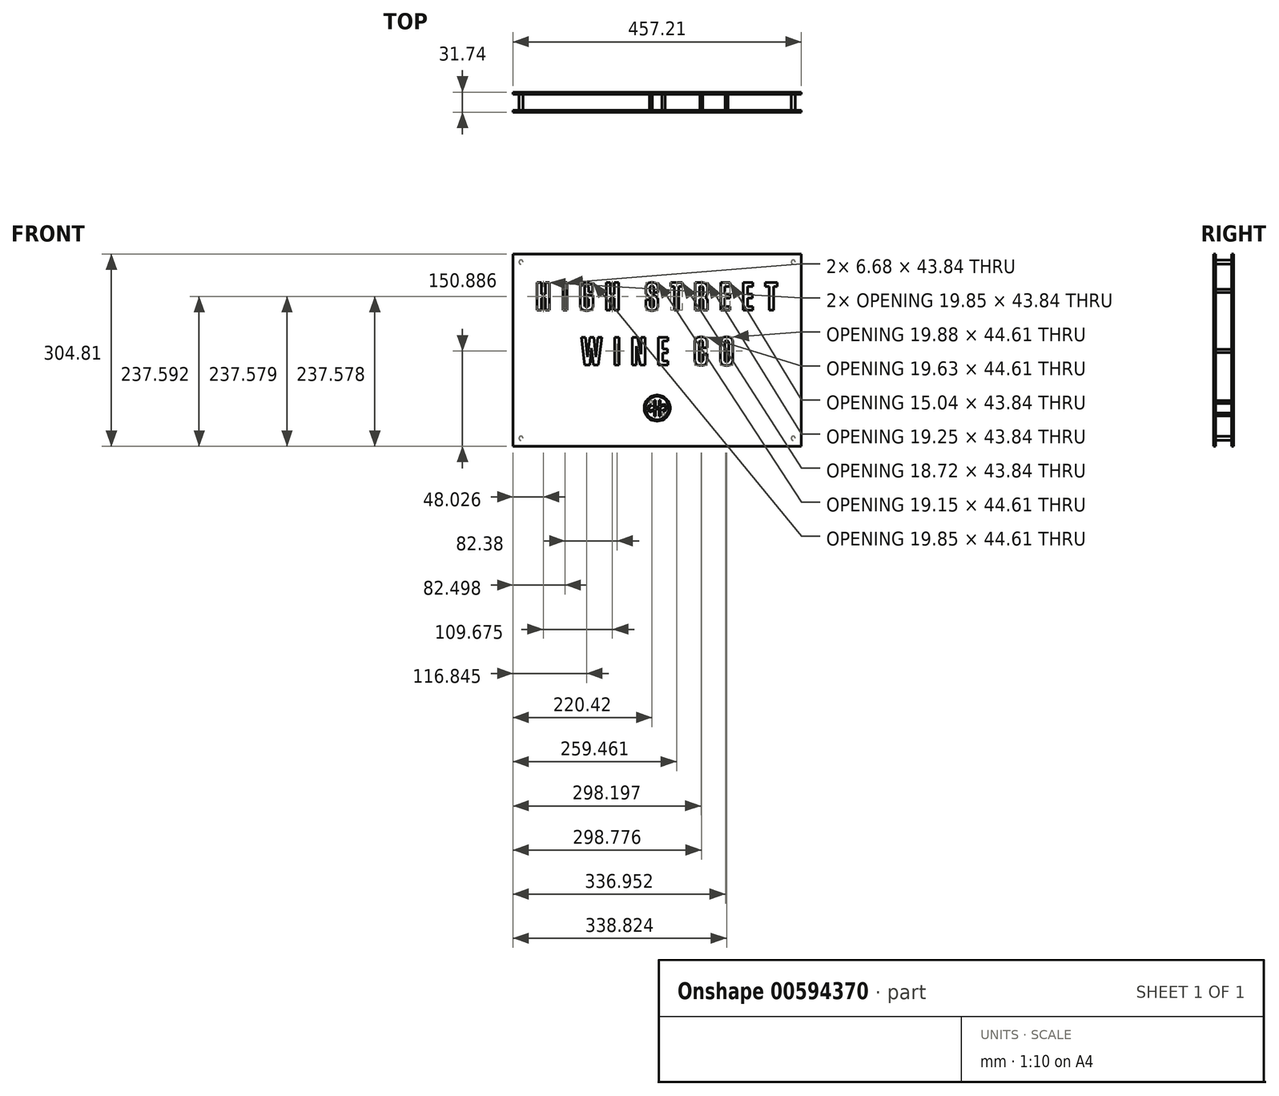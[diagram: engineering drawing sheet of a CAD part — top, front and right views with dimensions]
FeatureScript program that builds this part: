
annotation { "Feature Type Name" : "Feature", "Feature Type Description" : "" }
export const myFeature = defineFeature(function(context is Context, id is Id, definition is map)
    precondition{}
    {
        {
            var Q0;
            Q0=qCreatedBy(makeId("Front.planeOp"),FACE);
            var sketch = newSketch(context, id + "F0", { "sketchPlane" : qUnion([Q0])});
            skLineSegment(sketch, "E0", {"start": v(-228.6, 152.4) * mm, "end": v(228.6, 152.4) * mm});
            skLineSegment(sketch, "E1", {"start": v(228.6, 152.4) * mm, "end": v(228.6, -152.4) * mm});
            skLineSegment(sketch, "E2", {"start": v(228.6, -152.4) * mm, "end": v(-228.6, -152.4) * mm});
            skLineSegment(sketch, "E3", {"start": v(-228.6, -152.4) * mm, "end": v(-228.6, 152.4) * mm});
            skLineSegment(sketch, "E4", {"start": v(-177.33, 88.62) * mm, "end": v(-177.33, 107.1) * mm});
            skLineSegment(sketch, "E5", {"start": v(-177.33, 107.1) * mm, "end": v(-170.65, 107.1) * mm});
            skLineSegment(sketch, "E6", {"start": v(-170.65, 107.1) * mm, "end": v(-170.65, 63.26) * mm});
            skLineSegment(sketch, "E7", {"start": v(-170.65, 63.26) * mm, "end": v(-177.33, 63.26) * mm});
            skLineSegment(sketch, "E8", {"start": v(-177.33, 63.26) * mm, "end": v(-177.33, 82.54) * mm});
            skLineSegment(sketch, "E9", {"start": v(-177.33, 82.54) * mm, "end": v(-183.81, 82.54) * mm});
            skLineSegment(sketch, "E10", {"start": v(-183.81, 82.54) * mm, "end": v(-183.81, 63.26) * mm});
            skLineSegment(sketch, "E11", {"start": v(-183.81, 63.26) * mm, "end": v(-190.5, 63.26) * mm});
            skLineSegment(sketch, "E12", {"start": v(-190.5, 63.26) * mm, "end": v(-190.5, 107.1) * mm});
            skLineSegment(sketch, "E13", {"start": v(-190.5, 107.1) * mm, "end": v(-183.81, 107.1) * mm});
            skLineSegment(sketch, "E14", {"start": v(-183.81, 107.1) * mm, "end": v(-183.81, 88.62) * mm});
            skLineSegment(sketch, "E15", {"start": v(-183.81, 88.62) * mm, "end": v(-177.33, 88.62) * mm});
            skLineSegment(sketch, "E16", {"start": v(-149.44, 107.1) * mm, "end": v(-142.76, 107.1) * mm});
            skLineSegment(sketch, "E17", {"start": v(-142.76, 107.1) * mm, "end": v(-142.76, 63.26) * mm});
            skLineSegment(sketch, "E18", {"start": v(-142.76, 63.26) * mm, "end": v(-149.44, 63.26) * mm});
            skLineSegment(sketch, "E19", {"start": v(-149.44, 63.26) * mm, "end": v(-149.44, 107.1) * mm});
            skLineSegment(sketch, "E20", {"start": v(-111.87, 81.41) * mm, "end": v(-111.87, 87.2) * mm});
            skLineSegment(sketch, "E21", {"start": v(-111.87, 87.2) * mm, "end": v(-101.83, 87.2) * mm});
            skLineSegment(sketch, "E22", {"start": v(-101.83, 87.2) * mm, "end": v(-101.83, 71.02) * mm});
            skLineSegment(sketch, "E23", {"start": v(-101.83, 71.02) * mm, "end": v(-101.83, 70.13) * mm});
            skLineSegment(sketch, "E24", {"start": v(-101.83, 70.13) * mm, "end": v(-102.34, 67.45) * mm});
            skLineSegment(sketch, "E25", {"start": v(-102.34, 67.45) * mm, "end": v(-103.86, 64.9) * mm});
            skLineSegment(sketch, "E26", {"start": v(-103.86, 64.9) * mm, "end": v(-106.41, 63.37) * mm});
            skLineSegment(sketch, "E27", {"start": v(-106.41, 63.37) * mm, "end": v(-109.1, 62.86) * mm});
            skLineSegment(sketch, "E28", {"start": v(-109.1, 62.86) * mm, "end": v(-110, 62.86) * mm});
            skLineSegment(sketch, "E29", {"start": v(-110, 62.86) * mm, "end": v(-113.54, 62.86) * mm});
            skLineSegment(sketch, "E30", {"start": v(-113.54, 62.86) * mm, "end": v(-114.44, 62.86) * mm});
            skLineSegment(sketch, "E31", {"start": v(-114.44, 62.86) * mm, "end": v(-117.1, 63.37) * mm});
            skLineSegment(sketch, "E32", {"start": v(-117.1, 63.37) * mm, "end": v(-119.65, 64.9) * mm});
            skLineSegment(sketch, "E33", {"start": v(-119.65, 64.9) * mm, "end": v(-121.17, 67.45) * mm});
            skLineSegment(sketch, "E34", {"start": v(-121.17, 67.45) * mm, "end": v(-121.68, 70.13) * mm});
            skLineSegment(sketch, "E35", {"start": v(-121.68, 70.13) * mm, "end": v(-121.68, 71.02) * mm});
            skLineSegment(sketch, "E36", {"start": v(-121.68, 71.02) * mm, "end": v(-121.68, 99.34) * mm});
            skLineSegment(sketch, "E37", {"start": v(-121.68, 99.34) * mm, "end": v(-121.68, 100.23) * mm});
            skLineSegment(sketch, "E38", {"start": v(-121.68, 100.23) * mm, "end": v(-121.17, 102.9) * mm});
            skLineSegment(sketch, "E39", {"start": v(-121.17, 102.9) * mm, "end": v(-119.65, 105.44) * mm});
            skLineSegment(sketch, "E40", {"start": v(-119.65, 105.44) * mm, "end": v(-117.1, 106.97) * mm});
            skLineSegment(sketch, "E41", {"start": v(-117.1, 106.97) * mm, "end": v(-114.44, 107.47) * mm});
            skLineSegment(sketch, "E42", {"start": v(-114.44, 107.47) * mm, "end": v(-113.54, 107.47) * mm});
            skLineSegment(sketch, "E43", {"start": v(-113.54, 107.47) * mm, "end": v(-110.04, 107.47) * mm});
            skLineSegment(sketch, "E44", {"start": v(-110.04, 107.47) * mm, "end": v(-109.15, 107.47) * mm});
            skLineSegment(sketch, "E45", {"start": v(-109.15, 107.47) * mm, "end": v(-106.48, 106.97) * mm});
            skLineSegment(sketch, "E46", {"start": v(-106.48, 106.97) * mm, "end": v(-103.96, 105.45) * mm});
            skLineSegment(sketch, "E47", {"start": v(-103.96, 105.45) * mm, "end": v(-102.46, 102.92) * mm});
            skLineSegment(sketch, "E48", {"start": v(-102.46, 102.92) * mm, "end": v(-101.96, 100.27) * mm});
            skLineSegment(sketch, "E49", {"start": v(-101.96, 100.27) * mm, "end": v(-101.96, 99.39) * mm});
            skLineSegment(sketch, "E50", {"start": v(-101.96, 99.39) * mm, "end": v(-101.96, 92.33) * mm});
            skLineSegment(sketch, "E51", {"start": v(-101.96, 92.33) * mm, "end": v(-108.54, 92.33) * mm});
            skLineSegment(sketch, "E52", {"start": v(-108.54, 92.33) * mm, "end": v(-108.54, 99.01) * mm});
            skLineSegment(sketch, "E53", {"start": v(-108.54, 99.01) * mm, "end": v(-108.54, 99.3) * mm});
            skLineSegment(sketch, "E54", {"start": v(-108.54, 99.3) * mm, "end": v(-108.7, 100.15) * mm});
            skLineSegment(sketch, "E55", {"start": v(-108.7, 100.15) * mm, "end": v(-109.15, 100.96) * mm});
            skLineSegment(sketch, "E56", {"start": v(-109.15, 100.96) * mm, "end": v(-109.93, 101.43) * mm});
            skLineSegment(sketch, "E57", {"start": v(-109.93, 101.43) * mm, "end": v(-110.77, 101.6) * mm});
            skLineSegment(sketch, "E58", {"start": v(-110.77, 101.6) * mm, "end": v(-111.04, 101.6) * mm});
            skLineSegment(sketch, "E59", {"start": v(-111.04, 101.6) * mm, "end": v(-112.44, 101.6) * mm});
            skLineSegment(sketch, "E60", {"start": v(-112.44, 101.6) * mm, "end": v(-112.73, 101.6) * mm});
            skLineSegment(sketch, "E61", {"start": v(-112.73, 101.6) * mm, "end": v(-113.58, 101.43) * mm});
            skLineSegment(sketch, "E62", {"start": v(-113.58, 101.43) * mm, "end": v(-114.38, 100.96) * mm});
            skLineSegment(sketch, "E63", {"start": v(-114.38, 100.96) * mm, "end": v(-114.85, 100.15) * mm});
            skLineSegment(sketch, "E64", {"start": v(-114.85, 100.15) * mm, "end": v(-115, 99.3) * mm});
            skLineSegment(sketch, "E65", {"start": v(-115, 99.3) * mm, "end": v(-115, 99.01) * mm});
            skLineSegment(sketch, "E66", {"start": v(-115, 99.01) * mm, "end": v(-115, 71.33) * mm});
            skLineSegment(sketch, "E67", {"start": v(-115, 71.33) * mm, "end": v(-115, 71.04) * mm});
            skLineSegment(sketch, "E68", {"start": v(-115, 71.04) * mm, "end": v(-114.85, 70.19) * mm});
            skLineSegment(sketch, "E69", {"start": v(-114.85, 70.19) * mm, "end": v(-114.38, 69.4) * mm});
            skLineSegment(sketch, "E70", {"start": v(-114.38, 69.4) * mm, "end": v(-113.58, 68.92) * mm});
            skLineSegment(sketch, "E71", {"start": v(-113.58, 68.92) * mm, "end": v(-112.73, 68.77) * mm});
            skLineSegment(sketch, "E72", {"start": v(-112.73, 68.77) * mm, "end": v(-112.44, 68.77) * mm});
            skLineSegment(sketch, "E73", {"start": v(-112.44, 68.77) * mm, "end": v(-110.94, 68.77) * mm});
            skLineSegment(sketch, "E74", {"start": v(-110.94, 68.77) * mm, "end": v(-110.66, 68.77) * mm});
            skLineSegment(sketch, "E75", {"start": v(-110.66, 68.77) * mm, "end": v(-109.8, 68.92) * mm});
            skLineSegment(sketch, "E76", {"start": v(-109.8, 68.92) * mm, "end": v(-109, 69.4) * mm});
            skLineSegment(sketch, "E77", {"start": v(-109, 69.4) * mm, "end": v(-108.52, 70.19) * mm});
            skLineSegment(sketch, "E78", {"start": v(-108.52, 70.19) * mm, "end": v(-108.36, 71.04) * mm});
            skLineSegment(sketch, "E79", {"start": v(-108.36, 71.04) * mm, "end": v(-108.36, 71.33) * mm});
            skLineSegment(sketch, "E80", {"start": v(-108.36, 71.33) * mm, "end": v(-108.36, 81.41) * mm});
            skLineSegment(sketch, "E81", {"start": v(-108.36, 81.41) * mm, "end": v(-111.87, 81.41) * mm});
            skLineSegment(sketch, "E82", {"start": v(-67.66, 88.62) * mm, "end": v(-67.66, 107.1) * mm});
            skLineSegment(sketch, "E83", {"start": v(-67.66, 107.1) * mm, "end": v(-60.97, 107.1) * mm});
            skLineSegment(sketch, "E84", {"start": v(-60.97, 107.1) * mm, "end": v(-60.97, 63.26) * mm});
            skLineSegment(sketch, "E85", {"start": v(-60.97, 63.26) * mm, "end": v(-67.66, 63.26) * mm});
            skLineSegment(sketch, "E86", {"start": v(-67.66, 63.26) * mm, "end": v(-67.66, 82.54) * mm});
            skLineSegment(sketch, "E87", {"start": v(-67.66, 82.54) * mm, "end": v(-74.14, 82.54) * mm});
            skLineSegment(sketch, "E88", {"start": v(-74.14, 82.54) * mm, "end": v(-74.14, 63.26) * mm});
            skLineSegment(sketch, "E89", {"start": v(-74.14, 63.26) * mm, "end": v(-80.83, 63.26) * mm});
            skLineSegment(sketch, "E90", {"start": v(-80.83, 63.26) * mm, "end": v(-80.83, 107.1) * mm});
            skLineSegment(sketch, "E91", {"start": v(-80.83, 107.1) * mm, "end": v(-74.14, 107.1) * mm});
            skLineSegment(sketch, "E92", {"start": v(-74.14, 107.1) * mm, "end": v(-74.14, 88.62) * mm});
            skLineSegment(sketch, "E93", {"start": v(-74.14, 88.62) * mm, "end": v(-67.66, 88.62) * mm});
            skLineSegment(sketch, "E94", {"start": v(1.4, 78.16) * mm, "end": v(1.4, 71.02) * mm});
            skLineSegment(sketch, "E95", {"start": v(1.4, 71.02) * mm, "end": v(1.4, 70.13) * mm});
            skLineSegment(sketch, "E96", {"start": v(1.4, 70.13) * mm, "end": v(0.9, 67.45) * mm});
            skLineSegment(sketch, "E97", {"start": v(0.9, 67.45) * mm, "end": v(-0.63, 64.9) * mm});
            skLineSegment(sketch, "E98", {"start": v(-0.63, 64.9) * mm, "end": v(-3.17, 63.37) * mm});
            skLineSegment(sketch, "E99", {"start": v(-3.17, 63.37) * mm, "end": v(-5.85, 62.86) * mm});
            skLineSegment(sketch, "E100", {"start": v(-5.85, 62.86) * mm, "end": v(-6.74, 62.86) * mm});
            skLineSegment(sketch, "E101", {"start": v(-6.74, 62.86) * mm, "end": v(-9.7, 62.86) * mm});
            skLineSegment(sketch, "E102", {"start": v(-9.7, 62.86) * mm, "end": v(-10.59, 62.86) * mm});
            skLineSegment(sketch, "E103", {"start": v(-10.59, 62.86) * mm, "end": v(-13.26, 63.37) * mm});
            skLineSegment(sketch, "E104", {"start": v(-13.26, 63.37) * mm, "end": v(-15.77, 64.89) * mm});
            skLineSegment(sketch, "E105", {"start": v(-15.77, 64.89) * mm, "end": v(-17.26, 67.42) * mm});
            skLineSegment(sketch, "E106", {"start": v(-17.26, 67.42) * mm, "end": v(-17.76, 70.07) * mm});
            skLineSegment(sketch, "E107", {"start": v(-17.76, 70.07) * mm, "end": v(-17.76, 70.95) * mm});
            skLineSegment(sketch, "E108", {"start": v(-17.76, 70.95) * mm, "end": v(-17.76, 80.24) * mm});
            skLineSegment(sketch, "E109", {"start": v(-17.76, 80.24) * mm, "end": v(-11.25, 80.24) * mm});
            skLineSegment(sketch, "E110", {"start": v(-11.25, 80.24) * mm, "end": v(-11.25, 71.2) * mm});
            skLineSegment(sketch, "E111", {"start": v(-11.25, 71.2) * mm, "end": v(-11.25, 70.93) * mm});
            skLineSegment(sketch, "E112", {"start": v(-11.25, 70.93) * mm, "end": v(-11.1, 70.1) * mm});
            skLineSegment(sketch, "E113", {"start": v(-11.1, 70.1) * mm, "end": v(-10.62, 69.32) * mm});
            skLineSegment(sketch, "E114", {"start": v(-10.62, 69.32) * mm, "end": v(-9.82, 68.85) * mm});
            skLineSegment(sketch, "E115", {"start": v(-9.82, 68.85) * mm, "end": v(-8.96, 68.7) * mm});
            skLineSegment(sketch, "E116", {"start": v(-8.96, 68.7) * mm, "end": v(-8.67, 68.7) * mm});
            skLineSegment(sketch, "E117", {"start": v(-8.67, 68.7) * mm, "end": v(-7.82, 68.7) * mm});
            skLineSegment(sketch, "E118", {"start": v(-7.82, 68.7) * mm, "end": v(-7.53, 68.7) * mm});
            skLineSegment(sketch, "E119", {"start": v(-7.53, 68.7) * mm, "end": v(-6.68, 68.85) * mm});
            skLineSegment(sketch, "E120", {"start": v(-6.68, 68.85) * mm, "end": v(-5.87, 69.32) * mm});
            skLineSegment(sketch, "E121", {"start": v(-5.87, 69.32) * mm, "end": v(-5.4, 70.1) * mm});
            skLineSegment(sketch, "E122", {"start": v(-5.4, 70.1) * mm, "end": v(-5.24, 70.93) * mm});
            skLineSegment(sketch, "E123", {"start": v(-5.24, 70.93) * mm, "end": v(-5.24, 71.2) * mm});
            skLineSegment(sketch, "E124", {"start": v(-5.24, 71.2) * mm, "end": v(-5.24, 77.23) * mm});
            skLineSegment(sketch, "E125", {"start": v(-5.24, 77.23) * mm, "end": v(-5.24, 77.53) * mm});
            skLineSegment(sketch, "E126", {"start": v(-5.24, 77.53) * mm, "end": v(-5.35, 78.41) * mm});
            skLineSegment(sketch, "E127", {"start": v(-5.35, 78.41) * mm, "end": v(-5.7, 79.33) * mm});
            skLineSegment(sketch, "E128", {"start": v(-5.7, 79.33) * mm, "end": v(-6.28, 80.08) * mm});
            skLineSegment(sketch, "E129", {"start": v(-6.28, 80.08) * mm, "end": v(-6.9, 80.63) * mm});
            skLineSegment(sketch, "E130", {"start": v(-6.9, 80.63) * mm, "end": v(-7.11, 80.79) * mm});
            skLineSegment(sketch, "E131", {"start": v(-7.11, 80.79) * mm, "end": v(-13.87, 85.75) * mm});
            skLineSegment(sketch, "E132", {"start": v(-13.87, 85.75) * mm, "end": v(-14.38, 86.1) * mm});
            skLineSegment(sketch, "E133", {"start": v(-14.38, 86.1) * mm, "end": v(-15.76, 87.35) * mm});
            skLineSegment(sketch, "E134", {"start": v(-15.76, 87.35) * mm, "end": v(-16.95, 89.06) * mm});
            skLineSegment(sketch, "E135", {"start": v(-16.95, 89.06) * mm, "end": v(-17.58, 91) * mm});
            skLineSegment(sketch, "E136", {"start": v(-17.58, 91) * mm, "end": v(-17.76, 92.73) * mm});
            skLineSegment(sketch, "E137", {"start": v(-17.76, 92.73) * mm, "end": v(-17.76, 93.3) * mm});
            skLineSegment(sketch, "E138", {"start": v(-17.76, 93.3) * mm, "end": v(-17.76, 99.34) * mm});
            skLineSegment(sketch, "E139", {"start": v(-17.76, 99.34) * mm, "end": v(-17.76, 100.23) * mm});
            skLineSegment(sketch, "E140", {"start": v(-17.76, 100.23) * mm, "end": v(-17.25, 102.9) * mm});
            skLineSegment(sketch, "E141", {"start": v(-17.25, 102.9) * mm, "end": v(-15.72, 105.44) * mm});
            skLineSegment(sketch, "E142", {"start": v(-15.72, 105.44) * mm, "end": v(-13.18, 106.97) * mm});
            skLineSegment(sketch, "E143", {"start": v(-13.18, 106.97) * mm, "end": v(-10.51, 107.47) * mm});
            skLineSegment(sketch, "E144", {"start": v(-10.51, 107.47) * mm, "end": v(-9.62, 107.47) * mm});
            skLineSegment(sketch, "E145", {"start": v(-9.62, 107.47) * mm, "end": v(-6.79, 107.47) * mm});
            skLineSegment(sketch, "E146", {"start": v(-6.79, 107.47) * mm, "end": v(-5.9, 107.47) * mm});
            skLineSegment(sketch, "E147", {"start": v(-5.9, 107.47) * mm, "end": v(-3.26, 106.97) * mm});
            skLineSegment(sketch, "E148", {"start": v(-3.26, 106.97) * mm, "end": v(-0.73, 105.45) * mm});
            skLineSegment(sketch, "E149", {"start": v(-0.73, 105.45) * mm, "end": v(0.79, 102.92) * mm});
            skLineSegment(sketch, "E150", {"start": v(0.79, 102.92) * mm, "end": v(1.3, 100.27) * mm});
            skLineSegment(sketch, "E151", {"start": v(1.3, 100.27) * mm, "end": v(1.3, 99.39) * mm});
            skLineSegment(sketch, "E152", {"start": v(1.3, 99.39) * mm, "end": v(1.3, 91.43) * mm});
            skLineSegment(sketch, "E153", {"start": v(1.3, 91.43) * mm, "end": v(-5.29, 91.43) * mm});
            skLineSegment(sketch, "E154", {"start": v(-5.29, 91.43) * mm, "end": v(-5.29, 99.14) * mm});
            skLineSegment(sketch, "E155", {"start": v(-5.29, 99.14) * mm, "end": v(-5.29, 99.42) * mm});
            skLineSegment(sketch, "E156", {"start": v(-5.29, 99.42) * mm, "end": v(-5.44, 100.25) * mm});
            skLineSegment(sketch, "E157", {"start": v(-5.44, 100.25) * mm, "end": v(-5.91, 101.03) * mm});
            skLineSegment(sketch, "E158", {"start": v(-5.91, 101.03) * mm, "end": v(-6.7, 101.49) * mm});
            skLineSegment(sketch, "E159", {"start": v(-6.7, 101.49) * mm, "end": v(-7.54, 101.64) * mm});
            skLineSegment(sketch, "E160", {"start": v(-7.54, 101.64) * mm, "end": v(-7.82, 101.64) * mm});
            skLineSegment(sketch, "E161", {"start": v(-7.82, 101.64) * mm, "end": v(-8.64, 101.64) * mm});
            skLineSegment(sketch, "E162", {"start": v(-8.64, 101.64) * mm, "end": v(-8.91, 101.64) * mm});
            skLineSegment(sketch, "E163", {"start": v(-8.91, 101.64) * mm, "end": v(-9.73, 101.49) * mm});
            skLineSegment(sketch, "E164", {"start": v(-9.73, 101.49) * mm, "end": v(-10.5, 101.03) * mm});
            skLineSegment(sketch, "E165", {"start": v(-10.5, 101.03) * mm, "end": v(-10.97, 100.25) * mm});
            skLineSegment(sketch, "E166", {"start": v(-10.97, 100.25) * mm, "end": v(-11.12, 99.42) * mm});
            skLineSegment(sketch, "E167", {"start": v(-11.12, 99.42) * mm, "end": v(-11.12, 99.14) * mm});
            skLineSegment(sketch, "E168", {"start": v(-11.12, 99.14) * mm, "end": v(-11.12, 94.26) * mm});
            skLineSegment(sketch, "E169", {"start": v(-11.12, 94.26) * mm, "end": v(-11.12, 93.96) * mm});
            skLineSegment(sketch, "E170", {"start": v(-11.12, 93.96) * mm, "end": v(-11, 93.05) * mm});
            skLineSegment(sketch, "E171", {"start": v(-11, 93.05) * mm, "end": v(-10.65, 92.12) * mm});
            skLineSegment(sketch, "E172", {"start": v(-10.65, 92.12) * mm, "end": v(-10.07, 91.36) * mm});
            skLineSegment(sketch, "E173", {"start": v(-10.07, 91.36) * mm, "end": v(-9.46, 90.83) * mm});
            skLineSegment(sketch, "E174", {"start": v(-9.46, 90.83) * mm, "end": v(-9.24, 90.67) * mm});
            skLineSegment(sketch, "E175", {"start": v(-9.24, 90.67) * mm, "end": v(-2.46, 85.75) * mm});
            skLineSegment(sketch, "E176", {"start": v(-2.46, 85.75) * mm, "end": v(-1.97, 85.39) * mm});
            skLineSegment(sketch, "E177", {"start": v(-1.97, 85.39) * mm, "end": v(-0.63, 84.16) * mm});
            skLineSegment(sketch, "E178", {"start": v(-0.63, 84.16) * mm, "end": v(0.56, 82.49) * mm});
            skLineSegment(sketch, "E179", {"start": v(0.56, 82.49) * mm, "end": v(1.2, 80.54) * mm});
            skLineSegment(sketch, "E180", {"start": v(1.2, 80.54) * mm, "end": v(1.4, 78.76) * mm});
            skLineSegment(sketch, "E181", {"start": v(1.4, 78.76) * mm, "end": v(1.4, 78.16) * mm});
            skLineSegment(sketch, "E182", {"start": v(27.5, 63.26) * mm, "end": v(27.5, 101.01) * mm});
            skLineSegment(sketch, "E183", {"start": v(27.5, 101.01) * mm, "end": v(21.5, 101.01) * mm});
            skLineSegment(sketch, "E184", {"start": v(21.5, 101.01) * mm, "end": v(21.5, 107.1) * mm});
            skLineSegment(sketch, "E185", {"start": v(21.5, 107.1) * mm, "end": v(40.22, 107.1) * mm});
            skLineSegment(sketch, "E186", {"start": v(40.22, 107.1) * mm, "end": v(40.22, 101.01) * mm});
            skLineSegment(sketch, "E187", {"start": v(40.22, 101.01) * mm, "end": v(34.22, 101.01) * mm});
            skLineSegment(sketch, "E188", {"start": v(34.22, 101.01) * mm, "end": v(34.22, 63.26) * mm});
            skLineSegment(sketch, "E189", {"start": v(34.22, 63.26) * mm, "end": v(27.5, 63.26) * mm});
            skLineSegment(sketch, "E190", {"start": v(70.54, 101.16) * mm, "end": v(67.26, 101.16) * mm});
            skLineSegment(sketch, "E191", {"start": v(67.26, 101.16) * mm, "end": v(67.26, 86.67) * mm});
            skLineSegment(sketch, "E192", {"start": v(67.26, 86.67) * mm, "end": v(70.29, 86.67) * mm});
            skLineSegment(sketch, "E193", {"start": v(70.29, 86.67) * mm, "end": v(70.6, 86.67) * mm});
            skLineSegment(sketch, "E194", {"start": v(70.6, 86.67) * mm, "end": v(71.5, 86.84) * mm});
            skLineSegment(sketch, "E195", {"start": v(71.5, 86.84) * mm, "end": v(72.35, 87.34) * mm});
            skLineSegment(sketch, "E196", {"start": v(72.35, 87.34) * mm, "end": v(72.85, 88.18) * mm});
            skLineSegment(sketch, "E197", {"start": v(72.85, 88.18) * mm, "end": v(73.02, 89.08) * mm});
            skLineSegment(sketch, "E198", {"start": v(73.02, 89.08) * mm, "end": v(73.02, 89.37) * mm});
            skLineSegment(sketch, "E199", {"start": v(73.02, 89.37) * mm, "end": v(73.02, 98.64) * mm});
            skLineSegment(sketch, "E200", {"start": v(73.02, 98.64) * mm, "end": v(73.02, 98.92) * mm});
            skLineSegment(sketch, "E201", {"start": v(73.02, 98.92) * mm, "end": v(72.86, 99.75) * mm});
            skLineSegment(sketch, "E202", {"start": v(72.86, 99.75) * mm, "end": v(72.4, 100.54) * mm});
            skLineSegment(sketch, "E203", {"start": v(72.4, 100.54) * mm, "end": v(71.63, 101) * mm});
            skLineSegment(sketch, "E204", {"start": v(71.63, 101) * mm, "end": v(70.81, 101.16) * mm});
            skLineSegment(sketch, "E205", {"start": v(70.81, 101.16) * mm, "end": v(70.54, 101.16) * mm});
            skLineSegment(sketch, "E206", {"start": v(79.8, 78.16) * mm, "end": v(79.8, 63.26) * mm});
            skLineSegment(sketch, "E207", {"start": v(79.8, 63.26) * mm, "end": v(73.12, 63.26) * mm});
            skLineSegment(sketch, "E208", {"start": v(73.12, 63.26) * mm, "end": v(73.12, 78.03) * mm});
            skLineSegment(sketch, "E209", {"start": v(73.12, 78.03) * mm, "end": v(73.12, 78.35) * mm});
            skLineSegment(sketch, "E210", {"start": v(73.12, 78.35) * mm, "end": v(72.95, 79.3) * mm});
            skLineSegment(sketch, "E211", {"start": v(72.95, 79.3) * mm, "end": v(72.43, 80.17) * mm});
            skLineSegment(sketch, "E212", {"start": v(72.43, 80.17) * mm, "end": v(71.54, 80.67) * mm});
            skLineSegment(sketch, "E213", {"start": v(71.54, 80.67) * mm, "end": v(70.6, 80.84) * mm});
            skLineSegment(sketch, "E214", {"start": v(70.6, 80.84) * mm, "end": v(70.29, 80.84) * mm});
            skLineSegment(sketch, "E215", {"start": v(70.29, 80.84) * mm, "end": v(67.26, 80.84) * mm});
            skLineSegment(sketch, "E216", {"start": v(67.26, 80.84) * mm, "end": v(67.26, 63.26) * mm});
            skLineSegment(sketch, "E217", {"start": v(67.26, 63.26) * mm, "end": v(60.55, 63.26) * mm});
            skLineSegment(sketch, "E218", {"start": v(60.55, 63.26) * mm, "end": v(60.55, 107.1) * mm});
            skLineSegment(sketch, "E219", {"start": v(60.55, 107.1) * mm, "end": v(71.6, 107.1) * mm});
            skLineSegment(sketch, "E220", {"start": v(71.6, 107.1) * mm, "end": v(72.48, 107.1) * mm});
            skLineSegment(sketch, "E221", {"start": v(72.48, 107.1) * mm, "end": v(75.17, 106.6) * mm});
            skLineSegment(sketch, "E222", {"start": v(75.17, 106.6) * mm, "end": v(77.7, 105.08) * mm});
            skLineSegment(sketch, "E223", {"start": v(77.7, 105.08) * mm, "end": v(79.22, 102.54) * mm});
            skLineSegment(sketch, "E224", {"start": v(79.22, 102.54) * mm, "end": v(79.73, 99.86) * mm});
            skLineSegment(sketch, "E225", {"start": v(79.73, 99.86) * mm, "end": v(79.73, 98.96) * mm});
            skLineSegment(sketch, "E226", {"start": v(79.73, 98.96) * mm, "end": v(79.73, 90.67) * mm});
            skLineSegment(sketch, "E227", {"start": v(79.73, 90.67) * mm, "end": v(79.73, 90.04) * mm});
            skLineSegment(sketch, "E228", {"start": v(79.73, 90.04) * mm, "end": v(79.47, 88.12) * mm});
            skLineSegment(sketch, "E229", {"start": v(79.47, 88.12) * mm, "end": v(78.73, 86.22) * mm});
            skLineSegment(sketch, "E230", {"start": v(78.73, 86.22) * mm, "end": v(77.54, 84.86) * mm});
            skLineSegment(sketch, "E231", {"start": v(77.54, 84.86) * mm, "end": v(76.35, 84.11) * mm});
            skLineSegment(sketch, "E232", {"start": v(76.35, 84.11) * mm, "end": v(75.92, 83.94) * mm});
            skLineSegment(sketch, "E233", {"start": v(75.92, 83.94) * mm, "end": v(76.38, 83.82) * mm});
            skLineSegment(sketch, "E234", {"start": v(76.38, 83.82) * mm, "end": v(77.69, 83.18) * mm});
            skLineSegment(sketch, "E235", {"start": v(77.69, 83.18) * mm, "end": v(78.9, 82) * mm});
            skLineSegment(sketch, "E236", {"start": v(78.9, 82) * mm, "end": v(79.58, 80.35) * mm});
            skLineSegment(sketch, "E237", {"start": v(79.58, 80.35) * mm, "end": v(79.8, 78.7) * mm});
            skLineSegment(sketch, "E238", {"start": v(79.8, 78.7) * mm, "end": v(79.8, 78.16) * mm});
            skLineSegment(sketch, "E239", {"start": v(115.75, 107.1) * mm, "end": v(115.75, 101.01) * mm});
            skLineSegment(sketch, "E240", {"start": v(115.75, 101.01) * mm, "end": v(107.56, 101.01) * mm});
            skLineSegment(sketch, "E241", {"start": v(107.56, 101.01) * mm, "end": v(107.56, 88.62) * mm});
            skLineSegment(sketch, "E242", {"start": v(107.56, 88.62) * mm, "end": v(115.45, 88.62) * mm});
            skLineSegment(sketch, "E243", {"start": v(115.45, 88.62) * mm, "end": v(115.45, 82.54) * mm});
            skLineSegment(sketch, "E244", {"start": v(115.45, 82.54) * mm, "end": v(107.56, 82.54) * mm});
            skLineSegment(sketch, "E245", {"start": v(107.56, 82.54) * mm, "end": v(107.56, 69.32) * mm});
            skLineSegment(sketch, "E246", {"start": v(107.56, 69.32) * mm, "end": v(115.87, 69.32) * mm});
            skLineSegment(sketch, "E247", {"start": v(115.87, 69.32) * mm, "end": v(115.87, 63.26) * mm});
            skLineSegment(sketch, "E248", {"start": v(115.87, 63.26) * mm, "end": v(100.83, 63.26) * mm});
            skLineSegment(sketch, "E249", {"start": v(100.83, 63.26) * mm, "end": v(100.83, 107.1) * mm});
            skLineSegment(sketch, "E250", {"start": v(100.83, 107.1) * mm, "end": v(115.75, 107.1) * mm});
            skLineSegment(sketch, "E251", {"start": v(151.63, 107.1) * mm, "end": v(151.63, 101.01) * mm});
            skLineSegment(sketch, "E252", {"start": v(151.63, 101.01) * mm, "end": v(143.41, 101.01) * mm});
            skLineSegment(sketch, "E253", {"start": v(143.41, 101.01) * mm, "end": v(143.41, 88.62) * mm});
            skLineSegment(sketch, "E254", {"start": v(143.41, 88.62) * mm, "end": v(151.3, 88.62) * mm});
            skLineSegment(sketch, "E255", {"start": v(151.3, 88.62) * mm, "end": v(151.3, 82.54) * mm});
            skLineSegment(sketch, "E256", {"start": v(151.3, 82.54) * mm, "end": v(143.41, 82.54) * mm});
            skLineSegment(sketch, "E257", {"start": v(143.41, 82.54) * mm, "end": v(143.41, 69.32) * mm});
            skLineSegment(sketch, "E258", {"start": v(143.41, 69.32) * mm, "end": v(151.73, 69.32) * mm});
            skLineSegment(sketch, "E259", {"start": v(151.73, 69.32) * mm, "end": v(151.73, 63.26) * mm});
            skLineSegment(sketch, "E260", {"start": v(151.73, 63.26) * mm, "end": v(136.7, 63.26) * mm});
            skLineSegment(sketch, "E261", {"start": v(136.7, 63.26) * mm, "end": v(136.7, 107.1) * mm});
            skLineSegment(sketch, "E262", {"start": v(136.7, 107.1) * mm, "end": v(151.63, 107.1) * mm});
            skLineSegment(sketch, "E263", {"start": v(177.79, 63.26) * mm, "end": v(177.79, 101.01) * mm});
            skLineSegment(sketch, "E264", {"start": v(177.79, 101.01) * mm, "end": v(171.75, 101.01) * mm});
            skLineSegment(sketch, "E265", {"start": v(171.75, 101.01) * mm, "end": v(171.75, 107.1) * mm});
            skLineSegment(sketch, "E266", {"start": v(171.75, 107.1) * mm, "end": v(190.5, 107.1) * mm});
            skLineSegment(sketch, "E267", {"start": v(190.5, 107.1) * mm, "end": v(190.5, 101.01) * mm});
            skLineSegment(sketch, "E268", {"start": v(190.5, 101.01) * mm, "end": v(184.47, 101.01) * mm});
            skLineSegment(sketch, "E269", {"start": v(184.47, 101.01) * mm, "end": v(184.47, 63.26) * mm});
            skLineSegment(sketch, "E270", {"start": v(184.47, 63.26) * mm, "end": v(177.79, 63.26) * mm});
            skLineSegment(sketch, "E271", {"start": v(-97.06, -10.84) * mm, "end": v(-93.93, 20.4) * mm});
            skLineSegment(sketch, "E272", {"start": v(-93.93, 20.4) * mm, "end": v(-87.8, 20.4) * mm});
            skLineSegment(sketch, "E273", {"start": v(-87.8, 20.4) * mm, "end": v(-93.12, -23.43) * mm});
            skLineSegment(sketch, "E274", {"start": v(-93.12, -23.43) * mm, "end": v(-100.99, -23.43) * mm});
            skLineSegment(sketch, "E275", {"start": v(-100.99, -23.43) * mm, "end": v(-103.99, 3) * mm});
            skLineSegment(sketch, "E276", {"start": v(-103.99, 3) * mm, "end": v(-106.9, -23.43) * mm});
            skLineSegment(sketch, "E277", {"start": v(-106.9, -23.43) * mm, "end": v(-114.83, -23.43) * mm});
            skLineSegment(sketch, "E278", {"start": v(-114.83, -23.43) * mm, "end": v(-120.16, 20.4) * mm});
            skLineSegment(sketch, "E279", {"start": v(-120.16, 20.4) * mm, "end": v(-113.4, 20.4) * mm});
            skLineSegment(sketch, "E280", {"start": v(-113.4, 20.4) * mm, "end": v(-110.27, -10.84) * mm});
            skLineSegment(sketch, "E281", {"start": v(-110.27, -10.84) * mm, "end": v(-106.9, 20.4) * mm});
            skLineSegment(sketch, "E282", {"start": v(-106.9, 20.4) * mm, "end": v(-100.43, 20.4) * mm});
            skLineSegment(sketch, "E283", {"start": v(-100.43, 20.4) * mm, "end": v(-97.06, -10.84) * mm});
            skLineSegment(sketch, "E284", {"start": v(-67.06, 20.4) * mm, "end": v(-60.38, 20.4) * mm});
            skLineSegment(sketch, "E285", {"start": v(-60.38, 20.4) * mm, "end": v(-60.38, -23.43) * mm});
            skLineSegment(sketch, "E286", {"start": v(-60.38, -23.43) * mm, "end": v(-67.06, -23.43) * mm});
            skLineSegment(sketch, "E287", {"start": v(-67.06, -23.43) * mm, "end": v(-67.06, 20.4) * mm});
            skLineSegment(sketch, "E288", {"start": v(-26.49, -23.43) * mm, "end": v(-33.3, 6.06) * mm});
            skLineSegment(sketch, "E289", {"start": v(-33.3, 6.06) * mm, "end": v(-33.24, -1.65) * mm});
            skLineSegment(sketch, "E290", {"start": v(-33.24, -1.65) * mm, "end": v(-33.24, -23.43) * mm});
            skLineSegment(sketch, "E291", {"start": v(-33.24, -23.43) * mm, "end": v(-39.25, -23.43) * mm});
            skLineSegment(sketch, "E292", {"start": v(-39.25, -23.43) * mm, "end": v(-39.25, 20.4) * mm});
            skLineSegment(sketch, "E293", {"start": v(-39.25, 20.4) * mm, "end": v(-31.42, 20.4) * mm});
            skLineSegment(sketch, "E294", {"start": v(-31.42, 20.4) * mm, "end": v(-25.16, -6.63) * mm});
            skLineSegment(sketch, "E295", {"start": v(-25.16, -6.63) * mm, "end": v(-25.2, 0.68) * mm});
            skLineSegment(sketch, "E296", {"start": v(-25.2, 0.68) * mm, "end": v(-25.2, 20.4) * mm});
            skLineSegment(sketch, "E297", {"start": v(-25.2, 20.4) * mm, "end": v(-19.2, 20.4) * mm});
            skLineSegment(sketch, "E298", {"start": v(-19.2, 20.4) * mm, "end": v(-19.2, -23.43) * mm});
            skLineSegment(sketch, "E299", {"start": v(-19.2, -23.43) * mm, "end": v(-26.49, -23.43) * mm});
            skLineSegment(sketch, "E300", {"start": v(79.41, -5.45) * mm, "end": v(79.41, -15.67) * mm});
            skLineSegment(sketch, "E301", {"start": v(79.41, -15.67) * mm, "end": v(79.41, -16.56) * mm});
            skLineSegment(sketch, "E302", {"start": v(79.41, -16.56) * mm, "end": v(78.9, -19.25) * mm});
            skLineSegment(sketch, "E303", {"start": v(78.9, -19.25) * mm, "end": v(77.38, -21.8) * mm});
            skLineSegment(sketch, "E304", {"start": v(77.38, -21.8) * mm, "end": v(74.84, -23.32) * mm});
            skLineSegment(sketch, "E305", {"start": v(74.84, -23.32) * mm, "end": v(72.16, -23.83) * mm});
            skLineSegment(sketch, "E306", {"start": v(72.16, -23.83) * mm, "end": v(71.27, -23.83) * mm});
            skLineSegment(sketch, "E307", {"start": v(71.27, -23.83) * mm, "end": v(67.94, -23.83) * mm});
            skLineSegment(sketch, "E308", {"start": v(67.94, -23.83) * mm, "end": v(67.05, -23.83) * mm});
            skLineSegment(sketch, "E309", {"start": v(67.05, -23.83) * mm, "end": v(64.36, -23.32) * mm});
            skLineSegment(sketch, "E310", {"start": v(64.36, -23.32) * mm, "end": v(61.82, -21.8) * mm});
            skLineSegment(sketch, "E311", {"start": v(61.82, -21.8) * mm, "end": v(60.3, -19.25) * mm});
            skLineSegment(sketch, "E312", {"start": v(60.3, -19.25) * mm, "end": v(59.78, -16.56) * mm});
            skLineSegment(sketch, "E313", {"start": v(59.78, -16.56) * mm, "end": v(59.78, -15.67) * mm});
            skLineSegment(sketch, "E314", {"start": v(59.78, -15.67) * mm, "end": v(59.78, 12.64) * mm});
            skLineSegment(sketch, "E315", {"start": v(59.78, 12.64) * mm, "end": v(59.78, 13.54) * mm});
            skLineSegment(sketch, "E316", {"start": v(59.78, 13.54) * mm, "end": v(60.3, 16.2) * mm});
            skLineSegment(sketch, "E317", {"start": v(60.3, 16.2) * mm, "end": v(61.82, 18.75) * mm});
            skLineSegment(sketch, "E318", {"start": v(61.82, 18.75) * mm, "end": v(64.36, 20.27) * mm});
            skLineSegment(sketch, "E319", {"start": v(64.36, 20.27) * mm, "end": v(67.05, 20.78) * mm});
            skLineSegment(sketch, "E320", {"start": v(67.05, 20.78) * mm, "end": v(67.94, 20.78) * mm});
            skLineSegment(sketch, "E321", {"start": v(67.94, 20.78) * mm, "end": v(71.2, 20.78) * mm});
            skLineSegment(sketch, "E322", {"start": v(71.2, 20.78) * mm, "end": v(72.09, 20.78) * mm});
            skLineSegment(sketch, "E323", {"start": v(72.09, 20.78) * mm, "end": v(74.75, 20.29) * mm});
            skLineSegment(sketch, "E324", {"start": v(74.75, 20.29) * mm, "end": v(77.28, 18.78) * mm});
            skLineSegment(sketch, "E325", {"start": v(77.28, 18.78) * mm, "end": v(78.78, 16.26) * mm});
            skLineSegment(sketch, "E326", {"start": v(78.78, 16.26) * mm, "end": v(79.28, 13.59) * mm});
            skLineSegment(sketch, "E327", {"start": v(79.28, 13.59) * mm, "end": v(79.28, 12.7) * mm});
            skLineSegment(sketch, "E328", {"start": v(79.28, 12.7) * mm, "end": v(79.28, 3.73) * mm});
            skLineSegment(sketch, "E329", {"start": v(79.28, 3.73) * mm, "end": v(72.7, 3.73) * mm});
            skLineSegment(sketch, "E330", {"start": v(72.7, 3.73) * mm, "end": v(72.7, 12.32) * mm});
            skLineSegment(sketch, "E331", {"start": v(72.7, 12.32) * mm, "end": v(72.7, 12.6) * mm});
            skLineSegment(sketch, "E332", {"start": v(72.7, 12.6) * mm, "end": v(72.54, 13.46) * mm});
            skLineSegment(sketch, "E333", {"start": v(72.54, 13.46) * mm, "end": v(72.07, 14.27) * mm});
            skLineSegment(sketch, "E334", {"start": v(72.07, 14.27) * mm, "end": v(71.3, 14.74) * mm});
            skLineSegment(sketch, "E335", {"start": v(71.3, 14.74) * mm, "end": v(70.47, 14.9) * mm});
            skLineSegment(sketch, "E336", {"start": v(70.47, 14.9) * mm, "end": v(70.2, 14.9) * mm});
            skLineSegment(sketch, "E337", {"start": v(70.2, 14.9) * mm, "end": v(69.07, 14.9) * mm});
            skLineSegment(sketch, "E338", {"start": v(69.07, 14.9) * mm, "end": v(68.78, 14.9) * mm});
            skLineSegment(sketch, "E339", {"start": v(68.78, 14.9) * mm, "end": v(67.93, 14.74) * mm});
            skLineSegment(sketch, "E340", {"start": v(67.93, 14.74) * mm, "end": v(67.12, 14.27) * mm});
            skLineSegment(sketch, "E341", {"start": v(67.12, 14.27) * mm, "end": v(66.65, 13.46) * mm});
            skLineSegment(sketch, "E342", {"start": v(66.65, 13.46) * mm, "end": v(66.5, 12.6) * mm});
            skLineSegment(sketch, "E343", {"start": v(66.5, 12.6) * mm, "end": v(66.5, 12.32) * mm});
            skLineSegment(sketch, "E344", {"start": v(66.5, 12.32) * mm, "end": v(66.5, -15.37) * mm});
            skLineSegment(sketch, "E345", {"start": v(66.5, -15.37) * mm, "end": v(66.5, -15.65) * mm});
            skLineSegment(sketch, "E346", {"start": v(66.5, -15.65) * mm, "end": v(66.65, -16.5) * mm});
            skLineSegment(sketch, "E347", {"start": v(66.65, -16.5) * mm, "end": v(67.12, -17.3) * mm});
            skLineSegment(sketch, "E348", {"start": v(67.12, -17.3) * mm, "end": v(67.93, -17.77) * mm});
            skLineSegment(sketch, "E349", {"start": v(67.93, -17.77) * mm, "end": v(68.78, -17.92) * mm});
            skLineSegment(sketch, "E350", {"start": v(68.78, -17.92) * mm, "end": v(69.07, -17.92) * mm});
            skLineSegment(sketch, "E351", {"start": v(69.07, -17.92) * mm, "end": v(70.32, -17.92) * mm});
            skLineSegment(sketch, "E352", {"start": v(70.32, -17.92) * mm, "end": v(70.6, -17.92) * mm});
            skLineSegment(sketch, "E353", {"start": v(70.6, -17.92) * mm, "end": v(71.42, -17.77) * mm});
            skLineSegment(sketch, "E354", {"start": v(71.42, -17.77) * mm, "end": v(72.2, -17.3) * mm});
            skLineSegment(sketch, "E355", {"start": v(72.2, -17.3) * mm, "end": v(72.67, -16.5) * mm});
            skLineSegment(sketch, "E356", {"start": v(72.67, -16.5) * mm, "end": v(72.83, -15.65) * mm});
            skLineSegment(sketch, "E357", {"start": v(72.83, -15.65) * mm, "end": v(72.83, -15.37) * mm});
            skLineSegment(sketch, "E358", {"start": v(72.83, -15.37) * mm, "end": v(72.83, -5.45) * mm});
            skLineSegment(sketch, "E359", {"start": v(72.83, -5.45) * mm, "end": v(79.41, -5.45) * mm});
            skLineSegment(sketch, "E360", {"start": v(110.95, 14.9) * mm, "end": v(109.57, 14.9) * mm});
            skLineSegment(sketch, "E361", {"start": v(109.57, 14.9) * mm, "end": v(109.29, 14.9) * mm});
            skLineSegment(sketch, "E362", {"start": v(109.29, 14.9) * mm, "end": v(108.43, 14.74) * mm});
            skLineSegment(sketch, "E363", {"start": v(108.43, 14.74) * mm, "end": v(107.63, 14.27) * mm});
            skLineSegment(sketch, "E364", {"start": v(107.63, 14.27) * mm, "end": v(107.15, 13.46) * mm});
            skLineSegment(sketch, "E365", {"start": v(107.15, 13.46) * mm, "end": v(107, 12.6) * mm});
            skLineSegment(sketch, "E366", {"start": v(107, 12.6) * mm, "end": v(107, 12.32) * mm});
            skLineSegment(sketch, "E367", {"start": v(107, 12.32) * mm, "end": v(107, -15.37) * mm});
            skLineSegment(sketch, "E368", {"start": v(107, -15.37) * mm, "end": v(107, -15.65) * mm});
            skLineSegment(sketch, "E369", {"start": v(107, -15.65) * mm, "end": v(107.15, -16.5) * mm});
            skLineSegment(sketch, "E370", {"start": v(107.15, -16.5) * mm, "end": v(107.63, -17.3) * mm});
            skLineSegment(sketch, "E371", {"start": v(107.63, -17.3) * mm, "end": v(108.43, -17.77) * mm});
            skLineSegment(sketch, "E372", {"start": v(108.43, -17.77) * mm, "end": v(109.29, -17.92) * mm});
            skLineSegment(sketch, "E373", {"start": v(109.29, -17.92) * mm, "end": v(109.57, -17.92) * mm});
            skLineSegment(sketch, "E374", {"start": v(109.57, -17.92) * mm, "end": v(110.95, -17.92) * mm});
            skLineSegment(sketch, "E375", {"start": v(110.95, -17.92) * mm, "end": v(111.23, -17.92) * mm});
            skLineSegment(sketch, "E376", {"start": v(111.23, -17.92) * mm, "end": v(112.06, -17.77) * mm});
            skLineSegment(sketch, "E377", {"start": v(112.06, -17.77) * mm, "end": v(112.85, -17.3) * mm});
            skLineSegment(sketch, "E378", {"start": v(112.85, -17.3) * mm, "end": v(113.32, -16.5) * mm});
            skLineSegment(sketch, "E379", {"start": v(113.32, -16.5) * mm, "end": v(113.48, -15.65) * mm});
            skLineSegment(sketch, "E380", {"start": v(113.48, -15.65) * mm, "end": v(113.48, -15.37) * mm});
            skLineSegment(sketch, "E381", {"start": v(113.48, -15.37) * mm, "end": v(113.48, 12.32) * mm});
            skLineSegment(sketch, "E382", {"start": v(113.48, 12.32) * mm, "end": v(113.48, 12.6) * mm});
            skLineSegment(sketch, "E383", {"start": v(113.48, 12.6) * mm, "end": v(113.32, 13.46) * mm});
            skLineSegment(sketch, "E384", {"start": v(113.32, 13.46) * mm, "end": v(112.85, 14.27) * mm});
            skLineSegment(sketch, "E385", {"start": v(112.85, 14.27) * mm, "end": v(112.06, 14.74) * mm});
            skLineSegment(sketch, "E386", {"start": v(112.06, 14.74) * mm, "end": v(111.23, 14.9) * mm});
            skLineSegment(sketch, "E387", {"start": v(111.23, 14.9) * mm, "end": v(110.95, 14.9) * mm});
            skLineSegment(sketch, "E388", {"start": v(112.03, -23.83) * mm, "end": v(108.47, -23.83) * mm});
            skLineSegment(sketch, "E389", {"start": v(108.47, -23.83) * mm, "end": v(107.58, -23.83) * mm});
            skLineSegment(sketch, "E390", {"start": v(107.58, -23.83) * mm, "end": v(104.88, -23.32) * mm});
            skLineSegment(sketch, "E391", {"start": v(104.88, -23.32) * mm, "end": v(102.32, -21.8) * mm});
            skLineSegment(sketch, "E392", {"start": v(102.32, -21.8) * mm, "end": v(100.8, -19.24) * mm});
            skLineSegment(sketch, "E393", {"start": v(100.8, -19.24) * mm, "end": v(100.29, -16.56) * mm});
            skLineSegment(sketch, "E394", {"start": v(100.29, -16.56) * mm, "end": v(100.29, -15.67) * mm});
            skLineSegment(sketch, "E395", {"start": v(100.29, -15.67) * mm, "end": v(100.29, 12.64) * mm});
            skLineSegment(sketch, "E396", {"start": v(100.29, 12.64) * mm, "end": v(100.29, 13.54) * mm});
            skLineSegment(sketch, "E397", {"start": v(100.29, 13.54) * mm, "end": v(100.8, 16.2) * mm});
            skLineSegment(sketch, "E398", {"start": v(100.8, 16.2) * mm, "end": v(102.32, 18.75) * mm});
            skLineSegment(sketch, "E399", {"start": v(102.32, 18.75) * mm, "end": v(104.88, 20.27) * mm});
            skLineSegment(sketch, "E400", {"start": v(104.88, 20.27) * mm, "end": v(107.58, 20.78) * mm});
            skLineSegment(sketch, "E401", {"start": v(107.58, 20.78) * mm, "end": v(108.47, 20.78) * mm});
            skLineSegment(sketch, "E402", {"start": v(108.47, 20.78) * mm, "end": v(112.03, 20.78) * mm});
            skLineSegment(sketch, "E403", {"start": v(112.03, 20.78) * mm, "end": v(112.92, 20.78) * mm});
            skLineSegment(sketch, "E404", {"start": v(112.92, 20.78) * mm, "end": v(115.6, 20.27) * mm});
            skLineSegment(sketch, "E405", {"start": v(115.6, 20.27) * mm, "end": v(118.13, 18.75) * mm});
            skLineSegment(sketch, "E406", {"start": v(118.13, 18.75) * mm, "end": v(119.65, 16.2) * mm});
            skLineSegment(sketch, "E407", {"start": v(119.65, 16.2) * mm, "end": v(120.16, 13.54) * mm});
            skLineSegment(sketch, "E408", {"start": v(120.16, 13.54) * mm, "end": v(120.16, 12.64) * mm});
            skLineSegment(sketch, "E409", {"start": v(120.16, 12.64) * mm, "end": v(120.16, -15.67) * mm});
            skLineSegment(sketch, "E410", {"start": v(120.16, -15.67) * mm, "end": v(120.16, -16.56) * mm});
            skLineSegment(sketch, "E411", {"start": v(120.16, -16.56) * mm, "end": v(119.65, -19.24) * mm});
            skLineSegment(sketch, "E412", {"start": v(119.65, -19.24) * mm, "end": v(118.13, -21.8) * mm});
            skLineSegment(sketch, "E413", {"start": v(118.13, -21.8) * mm, "end": v(115.6, -23.32) * mm});
            skLineSegment(sketch, "E414", {"start": v(115.6, -23.32) * mm, "end": v(112.92, -23.83) * mm});
            skLineSegment(sketch, "E415", {"start": v(112.92, -23.83) * mm, "end": v(112.03, -23.83) * mm});
            skLineSegment(sketch, "E416", {"start": v(16.87, 20.4) * mm, "end": v(16.87, 14.32) * mm});
            skLineSegment(sketch, "E417", {"start": v(16.87, 14.32) * mm, "end": v(8.69, 14.32) * mm});
            skLineSegment(sketch, "E418", {"start": v(8.69, 14.32) * mm, "end": v(8.69, 1.93) * mm});
            skLineSegment(sketch, "E419", {"start": v(8.69, 1.93) * mm, "end": v(16.57, 1.93) * mm});
            skLineSegment(sketch, "E420", {"start": v(16.57, 1.93) * mm, "end": v(16.57, -4.15) * mm});
            skLineSegment(sketch, "E421", {"start": v(16.57, -4.15) * mm, "end": v(8.69, -4.15) * mm});
            skLineSegment(sketch, "E422", {"start": v(8.69, -4.15) * mm, "end": v(8.69, -17.37) * mm});
            skLineSegment(sketch, "E423", {"start": v(8.69, -17.37) * mm, "end": v(17.02, -17.37) * mm});
            skLineSegment(sketch, "E424", {"start": v(17.02, -17.37) * mm, "end": v(17.02, -23.43) * mm});
            skLineSegment(sketch, "E425", {"start": v(17.02, -23.43) * mm, "end": v(1.98, -23.43) * mm});
            skLineSegment(sketch, "E426", {"start": v(1.98, -23.43) * mm, "end": v(1.98, 20.4) * mm});
            skLineSegment(sketch, "E427", {"start": v(1.98, 20.4) * mm, "end": v(16.87, 20.4) * mm});
            skLineSegment(sketch, "E428", {"start": v(15.09, -91.02) * mm, "end": v(15.09, -91.42) * mm});
            skLineSegment(sketch, "E429", {"start": v(15.09, -91.42) * mm, "end": v(14.97, -92.6) * mm});
            skLineSegment(sketch, "E430", {"start": v(14.97, -92.6) * mm, "end": v(14.64, -93.86) * mm});
            skLineSegment(sketch, "E431", {"start": v(14.64, -93.86) * mm, "end": v(14.17, -94.82) * mm});
            skLineSegment(sketch, "E432", {"start": v(14.17, -94.82) * mm, "end": v(13.62, -95.52) * mm});
            skLineSegment(sketch, "E433", {"start": v(13.62, -95.52) * mm, "end": v(13.04, -96) * mm});
            skLineSegment(sketch, "E434", {"start": v(13.04, -96) * mm, "end": v(12.5, -96.31) * mm});
            skLineSegment(sketch, "E435", {"start": v(12.5, -96.31) * mm, "end": v(12.05, -96.49) * mm});
            skLineSegment(sketch, "E436", {"start": v(12.05, -96.49) * mm, "end": v(11.83, -96.55) * mm});
            skLineSegment(sketch, "E437", {"start": v(11.83, -96.55) * mm, "end": v(11.75, -96.56) * mm});
            skLineSegment(sketch, "E438", {"start": v(11.75, -96.56) * mm, "end": v(11.72, -96.57) * mm});
            skLineSegment(sketch, "E439", {"start": v(11.72, -96.57) * mm, "end": v(11.38, -96.62) * mm});
            skLineSegment(sketch, "E440", {"start": v(11.38, -96.62) * mm, "end": v(10.88, -96.66) * mm});
            skLineSegment(sketch, "E441", {"start": v(10.88, -96.66) * mm, "end": v(10.72, -96.66) * mm});
            skLineSegment(sketch, "E442", {"start": v(10.72, -96.66) * mm, "end": v(10.5, -96.66) * mm});
            skLineSegment(sketch, "E443", {"start": v(10.5, -96.66) * mm, "end": v(9.84, -96.6) * mm});
            skLineSegment(sketch, "E444", {"start": v(9.84, -96.6) * mm, "end": v(8.97, -96.41) * mm});
            skLineSegment(sketch, "E445", {"start": v(8.97, -96.41) * mm, "end": v(8.79, -96.35) * mm});
            skLineSegment(sketch, "E446", {"start": v(8.79, -96.35) * mm, "end": v(8.79, -94.25) * mm});
            skLineSegment(sketch, "E447", {"start": v(8.79, -94.25) * mm, "end": v(9.02, -94.36) * mm});
            skLineSegment(sketch, "E448", {"start": v(9.02, -94.36) * mm, "end": v(9.77, -94.59) * mm});
            skLineSegment(sketch, "E449", {"start": v(9.77, -94.59) * mm, "end": v(10.56, -94.7) * mm});
            skLineSegment(sketch, "E450", {"start": v(10.56, -94.7) * mm, "end": v(11.1, -94.68) * mm});
            skLineSegment(sketch, "E451", {"start": v(11.1, -94.68) * mm, "end": v(11.3, -94.64) * mm});
            skLineSegment(sketch, "E452", {"start": v(11.3, -94.64) * mm, "end": v(11.3, -94.64) * mm});
            skLineSegment(sketch, "E453", {"start": v(11.3, -94.64) * mm, "end": v(11.4, -94.62) * mm});
            skLineSegment(sketch, "E454", {"start": v(11.4, -94.62) * mm, "end": v(11.44, -94.62) * mm});
            skLineSegment(sketch, "E455", {"start": v(11.44, -94.62) * mm, "end": v(11.47, -94.61) * mm});
            skLineSegment(sketch, "E456", {"start": v(11.47, -94.61) * mm, "end": v(11.57, -94.58) * mm});
            skLineSegment(sketch, "E457", {"start": v(11.57, -94.58) * mm, "end": v(11.78, -94.48) * mm});
            skLineSegment(sketch, "E458", {"start": v(11.78, -94.48) * mm, "end": v(12.05, -94.29) * mm});
            skLineSegment(sketch, "E459", {"start": v(12.05, -94.29) * mm, "end": v(12.35, -93.98) * mm});
            skLineSegment(sketch, "E460", {"start": v(12.35, -93.98) * mm, "end": v(12.64, -93.52) * mm});
            skLineSegment(sketch, "E461", {"start": v(12.64, -93.52) * mm, "end": v(12.89, -92.9) * mm});
            skLineSegment(sketch, "E462", {"start": v(12.89, -92.9) * mm, "end": v(13.06, -92.07) * mm});
            skLineSegment(sketch, "E463", {"start": v(13.06, -92.07) * mm, "end": v(13.12, -91.28) * mm});
            skLineSegment(sketch, "E464", {"start": v(13.12, -91.28) * mm, "end": v(13.12, -91.01) * mm});
            skLineSegment(sketch, "E465", {"start": v(13.12, -91.01) * mm, "end": v(13.12, -90.87) * mm});
            skLineSegment(sketch, "E466", {"start": v(13.12, -90.87) * mm, "end": v(13.08, -90.43) * mm});
            skLineSegment(sketch, "E467", {"start": v(13.08, -90.43) * mm, "end": v(12.9, -89.66) * mm});
            skLineSegment(sketch, "E468", {"start": v(12.9, -89.66) * mm, "end": v(12.53, -88.87) * mm});
            skLineSegment(sketch, "E469", {"start": v(12.53, -88.87) * mm, "end": v(12.11, -88.37) * mm});
            skLineSegment(sketch, "E470", {"start": v(12.11, -88.37) * mm, "end": v(11.94, -88.26) * mm});
            skLineSegment(sketch, "E471", {"start": v(11.94, -88.26) * mm, "end": v(11.74, -88.14) * mm});
            skLineSegment(sketch, "E472", {"start": v(11.74, -88.14) * mm, "end": v(11.02, -87.97) * mm});
            skLineSegment(sketch, "E473", {"start": v(11.02, -87.97) * mm, "end": v(9.95, -88.05) * mm});
            skLineSegment(sketch, "E474", {"start": v(9.95, -88.05) * mm, "end": v(8.83, -88.38) * mm});
            skLineSegment(sketch, "E475", {"start": v(8.83, -88.38) * mm, "end": v(8.05, -88.7) * mm});
            skLineSegment(sketch, "E476", {"start": v(8.05, -88.7) * mm, "end": v(7.8, -88.83) * mm});
            skLineSegment(sketch, "E477", {"start": v(7.8, -88.83) * mm, "end": v(4.92, -90.36) * mm});
            skLineSegment(sketch, "E478", {"start": v(4.92, -90.36) * mm, "end": v(4.92, -104.63) * mm});
            skLineSegment(sketch, "E479", {"start": v(4.92, -104.63) * mm, "end": v(2.95, -104.63) * mm});
            skLineSegment(sketch, "E480", {"start": v(2.95, -104.63) * mm, "end": v(2.95, -91.4) * mm});
            skLineSegment(sketch, "E481", {"start": v(2.95, -91.4) * mm, "end": v(-2.75, -94.43) * mm});
            skLineSegment(sketch, "E482", {"start": v(-2.75, -94.43) * mm, "end": v(-2.75, -104.63) * mm});
            skLineSegment(sketch, "E483", {"start": v(-2.75, -104.63) * mm, "end": v(-4.71, -104.63) * mm});
            skLineSegment(sketch, "E484", {"start": v(-4.71, -104.63) * mm, "end": v(-4.71, -95.47) * mm});
            skLineSegment(sketch, "E485", {"start": v(-4.71, -95.47) * mm, "end": v(-6.72, -96.53) * mm});
            skLineSegment(sketch, "E486", {"start": v(-6.72, -96.53) * mm, "end": v(-6.72, -96.53) * mm});
            skLineSegment(sketch, "E487", {"start": v(-6.72, -96.53) * mm, "end": v(-6.73, -96.53) * mm});
            skLineSegment(sketch, "E488", {"start": v(-6.73, -96.53) * mm, "end": v(-7.09, -96.71) * mm});
            skLineSegment(sketch, "E489", {"start": v(-7.09, -96.71) * mm, "end": v(-8.78, -97.33) * mm});
            skLineSegment(sketch, "E490", {"start": v(-8.78, -97.33) * mm, "end": v(-10.14, -97.6) * mm});
            skLineSegment(sketch, "E491", {"start": v(-10.14, -97.6) * mm, "end": v(-10.59, -97.6) * mm});
            skLineSegment(sketch, "E492", {"start": v(-10.59, -97.6) * mm, "end": v(-10.88, -97.6) * mm});
            skLineSegment(sketch, "E493", {"start": v(-10.88, -97.6) * mm, "end": v(-11.77, -97.45) * mm});
            skLineSegment(sketch, "E494", {"start": v(-11.77, -97.45) * mm, "end": v(-12.65, -97.1) * mm});
            skLineSegment(sketch, "E495", {"start": v(-12.65, -97.1) * mm, "end": v(-12.8, -97) * mm});
            skLineSegment(sketch, "E496", {"start": v(-12.8, -97) * mm, "end": v(-13, -96.88) * mm});
            skLineSegment(sketch, "E497", {"start": v(-13, -96.88) * mm, "end": v(-13.5, -96.43) * mm});
            skLineSegment(sketch, "E498", {"start": v(-13.5, -96.43) * mm, "end": v(-14.03, -95.76) * mm});
            skLineSegment(sketch, "E499", {"start": v(-14.03, -95.76) * mm, "end": v(-14.4, -95.05) * mm});
            skLineSegment(sketch, "E500", {"start": v(-14.4, -95.05) * mm, "end": v(-14.65, -94.34) * mm});
            skLineSegment(sketch, "E501", {"start": v(-14.65, -94.34) * mm, "end": v(-14.8, -93.68) * mm});
            skLineSegment(sketch, "E502", {"start": v(-14.8, -93.68) * mm, "end": v(-14.87, -93.14) * mm});
            skLineSegment(sketch, "E503", {"start": v(-14.87, -93.14) * mm, "end": v(-14.9, -92.75) * mm});
            skLineSegment(sketch, "E504", {"start": v(-14.9, -92.75) * mm, "end": v(-14.9, -92.63) * mm});
            skLineSegment(sketch, "E505", {"start": v(-14.9, -92.63) * mm, "end": v(-14.9, -92.58) * mm});
            skLineSegment(sketch, "E506", {"start": v(-14.9, -92.58) * mm, "end": v(-14.9, -92.19) * mm});
            skLineSegment(sketch, "E507", {"start": v(-14.9, -92.19) * mm, "end": v(-14.78, -91) * mm});
            skLineSegment(sketch, "E508", {"start": v(-14.78, -91) * mm, "end": v(-14.46, -89.74) * mm});
            skLineSegment(sketch, "E509", {"start": v(-14.46, -89.74) * mm, "end": v(-14, -88.78) * mm});
            skLineSegment(sketch, "E510", {"start": v(-14, -88.78) * mm, "end": v(-13.44, -88.08) * mm});
            skLineSegment(sketch, "E511", {"start": v(-13.44, -88.08) * mm, "end": v(-12.86, -87.6) * mm});
            skLineSegment(sketch, "E512", {"start": v(-12.86, -87.6) * mm, "end": v(-12.32, -87.29) * mm});
            skLineSegment(sketch, "E513", {"start": v(-12.32, -87.29) * mm, "end": v(-11.87, -87.11) * mm});
            skLineSegment(sketch, "E514", {"start": v(-11.87, -87.11) * mm, "end": v(-11.64, -87.05) * mm});
            skLineSegment(sketch, "E515", {"start": v(-11.64, -87.05) * mm, "end": v(-11.57, -87.04) * mm});
            skLineSegment(sketch, "E516", {"start": v(-11.57, -87.04) * mm, "end": v(-11.5, -87.02) * mm});
            skLineSegment(sketch, "E517", {"start": v(-11.5, -87.02) * mm, "end": v(-11.2, -86.98) * mm});
            skLineSegment(sketch, "E518", {"start": v(-11.2, -86.98) * mm, "end": v(-10.55, -86.94) * mm});
            skLineSegment(sketch, "E519", {"start": v(-10.55, -86.94) * mm, "end": v(-9.67, -87) * mm});
            skLineSegment(sketch, "E520", {"start": v(-9.67, -87) * mm, "end": v(-8.87, -87.17) * mm});
            skLineSegment(sketch, "E521", {"start": v(-8.87, -87.17) * mm, "end": v(-8.6, -87.25) * mm});
            skLineSegment(sketch, "E522", {"start": v(-8.6, -87.25) * mm, "end": v(-8.6, -89.36) * mm});
            skLineSegment(sketch, "E523", {"start": v(-8.6, -89.36) * mm, "end": v(-8.84, -89.25) * mm});
            skLineSegment(sketch, "E524", {"start": v(-8.84, -89.25) * mm, "end": v(-9.59, -89.01) * mm});
            skLineSegment(sketch, "E525", {"start": v(-9.59, -89.01) * mm, "end": v(-10.38, -88.9) * mm});
            skLineSegment(sketch, "E526", {"start": v(-10.38, -88.9) * mm, "end": v(-10.91, -88.92) * mm});
            skLineSegment(sketch, "E527", {"start": v(-10.91, -88.92) * mm, "end": v(-11.12, -88.96) * mm});
            skLineSegment(sketch, "E528", {"start": v(-11.12, -88.96) * mm, "end": v(-11.13, -88.96) * mm});
            skLineSegment(sketch, "E529", {"start": v(-11.13, -88.96) * mm, "end": v(-11.22, -88.99) * mm});
            skLineSegment(sketch, "E530", {"start": v(-11.22, -88.99) * mm, "end": v(-11.25, -88.99) * mm});
            skLineSegment(sketch, "E531", {"start": v(-11.25, -88.99) * mm, "end": v(-11.29, -89) * mm});
            skLineSegment(sketch, "E532", {"start": v(-11.29, -89) * mm, "end": v(-11.38, -89.02) * mm});
            skLineSegment(sketch, "E533", {"start": v(-11.38, -89.02) * mm, "end": v(-11.6, -89.13) * mm});
            skLineSegment(sketch, "E534", {"start": v(-11.6, -89.13) * mm, "end": v(-11.87, -89.32) * mm});
            skLineSegment(sketch, "E535", {"start": v(-11.87, -89.32) * mm, "end": v(-12.17, -89.63) * mm});
            skLineSegment(sketch, "E536", {"start": v(-12.17, -89.63) * mm, "end": v(-12.46, -90.08) * mm});
            skLineSegment(sketch, "E537", {"start": v(-12.46, -90.08) * mm, "end": v(-12.7, -90.71) * mm});
            skLineSegment(sketch, "E538", {"start": v(-12.7, -90.71) * mm, "end": v(-12.88, -91.54) * mm});
            skLineSegment(sketch, "E539", {"start": v(-12.88, -91.54) * mm, "end": v(-12.94, -92.33) * mm});
            skLineSegment(sketch, "E540", {"start": v(-12.94, -92.33) * mm, "end": v(-12.94, -92.59) * mm});
            skLineSegment(sketch, "E541", {"start": v(-12.94, -92.59) * mm, "end": v(-12.94, -92.73) * mm});
            skLineSegment(sketch, "E542", {"start": v(-12.94, -92.73) * mm, "end": v(-12.9, -93.17) * mm});
            skLineSegment(sketch, "E543", {"start": v(-12.9, -93.17) * mm, "end": v(-12.72, -93.94) * mm});
            skLineSegment(sketch, "E544", {"start": v(-12.72, -93.94) * mm, "end": v(-12.36, -94.73) * mm});
            skLineSegment(sketch, "E545", {"start": v(-12.36, -94.73) * mm, "end": v(-11.94, -95.23) * mm});
            skLineSegment(sketch, "E546", {"start": v(-11.94, -95.23) * mm, "end": v(-11.76, -95.34) * mm});
            skLineSegment(sketch, "E547", {"start": v(-11.76, -95.34) * mm, "end": v(-11.56, -95.46) * mm});
            skLineSegment(sketch, "E548", {"start": v(-11.56, -95.46) * mm, "end": v(-10.83, -95.62) * mm});
            skLineSegment(sketch, "E549", {"start": v(-10.83, -95.62) * mm, "end": v(-9.76, -95.55) * mm});
            skLineSegment(sketch, "E550", {"start": v(-9.76, -95.55) * mm, "end": v(-8.65, -95.22) * mm});
            skLineSegment(sketch, "E551", {"start": v(-8.65, -95.22) * mm, "end": v(-7.87, -94.9) * mm});
            skLineSegment(sketch, "E552", {"start": v(-7.87, -94.9) * mm, "end": v(-7.61, -94.77) * mm});
            skLineSegment(sketch, "E553", {"start": v(-7.61, -94.77) * mm, "end": v(-4.71, -93.23) * mm});
            skLineSegment(sketch, "E554", {"start": v(-4.71, -93.23) * mm, "end": v(-4.71, -79.08) * mm});
            skLineSegment(sketch, "E555", {"start": v(-4.71, -79.08) * mm, "end": v(-2.75, -79.08) * mm});
            skLineSegment(sketch, "E556", {"start": v(-2.75, -79.08) * mm, "end": v(-2.75, -92.2) * mm});
            skLineSegment(sketch, "E557", {"start": v(-2.75, -92.2) * mm, "end": v(2.95, -89.17) * mm});
            skLineSegment(sketch, "E558", {"start": v(2.95, -89.17) * mm, "end": v(2.95, -79.08) * mm});
            skLineSegment(sketch, "E559", {"start": v(2.95, -79.08) * mm, "end": v(4.92, -79.08) * mm});
            skLineSegment(sketch, "E560", {"start": v(4.92, -79.08) * mm, "end": v(4.92, -88.12) * mm});
            skLineSegment(sketch, "E561", {"start": v(4.92, -88.12) * mm, "end": v(6.9, -87.07) * mm});
            skLineSegment(sketch, "E562", {"start": v(6.9, -87.07) * mm, "end": v(6.9, -87.08) * mm});
            skLineSegment(sketch, "E563", {"start": v(6.9, -87.08) * mm, "end": v(6.91, -87.07) * mm});
            skLineSegment(sketch, "E564", {"start": v(6.91, -87.07) * mm, "end": v(7.55, -86.76) * mm});
            skLineSegment(sketch, "E565", {"start": v(7.55, -86.76) * mm, "end": v(10.34, -86.02) * mm});
            skLineSegment(sketch, "E566", {"start": v(10.34, -86.02) * mm, "end": v(12.62, -86.37) * mm});
            skLineSegment(sketch, "E567", {"start": v(12.62, -86.37) * mm, "end": v(13, -86.6) * mm});
            skLineSegment(sketch, "E568", {"start": v(13, -86.6) * mm, "end": v(13.18, -86.72) * mm});
            skLineSegment(sketch, "E569", {"start": v(13.18, -86.72) * mm, "end": v(13.69, -87.17) * mm});
            skLineSegment(sketch, "E570", {"start": v(13.69, -87.17) * mm, "end": v(14.2, -87.84) * mm});
            skLineSegment(sketch, "E571", {"start": v(14.2, -87.84) * mm, "end": v(14.58, -88.55) * mm});
            skLineSegment(sketch, "E572", {"start": v(14.58, -88.55) * mm, "end": v(14.83, -89.26) * mm});
            skLineSegment(sketch, "E573", {"start": v(14.83, -89.26) * mm, "end": v(14.98, -89.92) * mm});
            skLineSegment(sketch, "E574", {"start": v(14.98, -89.92) * mm, "end": v(15.06, -90.46) * mm});
            skLineSegment(sketch, "E575", {"start": v(15.06, -90.46) * mm, "end": v(15.09, -90.85) * mm});
            skLineSegment(sketch, "E576", {"start": v(15.09, -90.85) * mm, "end": v(15.09, -90.98) * mm});
            skLineSegment(sketch, "E577", {"start": v(15.09, -90.98) * mm, "end": v(15.09, -91.02) * mm});
            skLineSegment(sketch, "E578", {"start": v(0, -110.52) * mm, "end": v(-0.94, -110.52) * mm});
            skLineSegment(sketch, "E579", {"start": v(-0.94, -110.52) * mm, "end": v(-3.76, -110.14) * mm});
            skLineSegment(sketch, "E580", {"start": v(-3.76, -110.14) * mm, "end": v(-7.26, -109.05) * mm});
            skLineSegment(sketch, "E581", {"start": v(-7.26, -109.05) * mm, "end": v(-10.43, -107.33) * mm});
            skLineSegment(sketch, "E582", {"start": v(-10.43, -107.33) * mm, "end": v(-13.2, -105.05) * mm});
            skLineSegment(sketch, "E583", {"start": v(-13.2, -105.05) * mm, "end": v(-15.47, -102.29) * mm});
            skLineSegment(sketch, "E584", {"start": v(-15.47, -102.29) * mm, "end": v(-17.2, -99.11) * mm});
            skLineSegment(sketch, "E585", {"start": v(-17.2, -99.11) * mm, "end": v(-18.28, -95.61) * mm});
            skLineSegment(sketch, "E586", {"start": v(-18.28, -95.61) * mm, "end": v(-18.66, -92.8) * mm});
            skLineSegment(sketch, "E587", {"start": v(-18.66, -92.8) * mm, "end": v(-18.66, -91.85) * mm});
            skLineSegment(sketch, "E588", {"start": v(-18.66, -91.85) * mm, "end": v(-18.66, -90.91) * mm});
            skLineSegment(sketch, "E589", {"start": v(-18.66, -90.91) * mm, "end": v(-18.28, -88.1) * mm});
            skLineSegment(sketch, "E590", {"start": v(-18.28, -88.1) * mm, "end": v(-17.2, -84.6) * mm});
            skLineSegment(sketch, "E591", {"start": v(-17.2, -84.6) * mm, "end": v(-15.47, -81.42) * mm});
            skLineSegment(sketch, "E592", {"start": v(-15.47, -81.42) * mm, "end": v(-13.2, -78.66) * mm});
            skLineSegment(sketch, "E593", {"start": v(-13.2, -78.66) * mm, "end": v(-10.43, -76.38) * mm});
            skLineSegment(sketch, "E594", {"start": v(-10.43, -76.38) * mm, "end": v(-7.26, -74.66) * mm});
            skLineSegment(sketch, "E595", {"start": v(-7.26, -74.66) * mm, "end": v(-3.76, -73.57) * mm});
            skLineSegment(sketch, "E596", {"start": v(-3.76, -73.57) * mm, "end": v(-0.94, -73.19) * mm});
            skLineSegment(sketch, "E597", {"start": v(-0.94, -73.19) * mm, "end": v(0, -73.19) * mm});
            skLineSegment(sketch, "E598", {"start": v(0, -73.19) * mm, "end": v(0.94, -73.19) * mm});
            skLineSegment(sketch, "E599", {"start": v(0.94, -73.19) * mm, "end": v(3.76, -73.57) * mm});
            skLineSegment(sketch, "E600", {"start": v(3.76, -73.57) * mm, "end": v(7.26, -74.66) * mm});
            skLineSegment(sketch, "E601", {"start": v(7.26, -74.66) * mm, "end": v(10.43, -76.38) * mm});
            skLineSegment(sketch, "E602", {"start": v(10.43, -76.38) * mm, "end": v(13.2, -78.66) * mm});
            skLineSegment(sketch, "E603", {"start": v(13.2, -78.66) * mm, "end": v(15.48, -81.42) * mm});
            skLineSegment(sketch, "E604", {"start": v(15.48, -81.42) * mm, "end": v(17.2, -84.6) * mm});
            skLineSegment(sketch, "E605", {"start": v(17.2, -84.6) * mm, "end": v(18.3, -88.1) * mm});
            skLineSegment(sketch, "E606", {"start": v(18.3, -88.1) * mm, "end": v(18.67, -90.91) * mm});
            skLineSegment(sketch, "E607", {"start": v(18.67, -90.91) * mm, "end": v(18.67, -91.85) * mm});
            skLineSegment(sketch, "E608", {"start": v(18.67, -91.85) * mm, "end": v(18.67, -92.8) * mm});
            skLineSegment(sketch, "E609", {"start": v(18.67, -92.8) * mm, "end": v(18.3, -95.61) * mm});
            skLineSegment(sketch, "E610", {"start": v(18.3, -95.61) * mm, "end": v(17.2, -99.11) * mm});
            skLineSegment(sketch, "E611", {"start": v(17.2, -99.11) * mm, "end": v(15.48, -102.29) * mm});
            skLineSegment(sketch, "E612", {"start": v(15.48, -102.29) * mm, "end": v(13.2, -105.05) * mm});
            skLineSegment(sketch, "E613", {"start": v(13.2, -105.05) * mm, "end": v(10.43, -107.33) * mm});
            skLineSegment(sketch, "E614", {"start": v(10.43, -107.33) * mm, "end": v(7.26, -109.05) * mm});
            skLineSegment(sketch, "E615", {"start": v(7.26, -109.05) * mm, "end": v(3.76, -110.14) * mm});
            skLineSegment(sketch, "E616", {"start": v(3.76, -110.14) * mm, "end": v(0.94, -110.52) * mm});
            skLineSegment(sketch, "E617", {"start": v(0.94, -110.52) * mm, "end": v(0, -110.52) * mm});
            skLineSegment(sketch, "E618", {"start": v(0, -71.22) * mm, "end": v(-1.04, -71.22) * mm});
            skLineSegment(sketch, "E619", {"start": v(-1.04, -71.22) * mm, "end": v(-4.15, -71.64) * mm});
            skLineSegment(sketch, "E620", {"start": v(-4.15, -71.64) * mm, "end": v(-8.02, -72.84) * mm});
            skLineSegment(sketch, "E621", {"start": v(-8.02, -72.84) * mm, "end": v(-11.53, -74.75) * mm});
            skLineSegment(sketch, "E622", {"start": v(-11.53, -74.75) * mm, "end": v(-14.58, -77.27) * mm});
            skLineSegment(sketch, "E623", {"start": v(-14.58, -77.27) * mm, "end": v(-17.1, -80.33) * mm});
            skLineSegment(sketch, "E624", {"start": v(-17.1, -80.33) * mm, "end": v(-19.01, -83.83) * mm});
            skLineSegment(sketch, "E625", {"start": v(-19.01, -83.83) * mm, "end": v(-20.22, -87.7) * mm});
            skLineSegment(sketch, "E626", {"start": v(-20.22, -87.7) * mm, "end": v(-20.64, -90.81) * mm});
            skLineSegment(sketch, "E627", {"start": v(-20.64, -90.81) * mm, "end": v(-20.64, -91.85) * mm});
            skLineSegment(sketch, "E628", {"start": v(-20.64, -91.85) * mm, "end": v(-20.64, -92.9) * mm});
            skLineSegment(sketch, "E629", {"start": v(-20.64, -92.9) * mm, "end": v(-20.22, -96) * mm});
            skLineSegment(sketch, "E630", {"start": v(-20.22, -96) * mm, "end": v(-19.01, -99.88) * mm});
            skLineSegment(sketch, "E631", {"start": v(-19.01, -99.88) * mm, "end": v(-17.1, -103.38) * mm});
            skLineSegment(sketch, "E632", {"start": v(-17.1, -103.38) * mm, "end": v(-14.58, -106.44) * mm});
            skLineSegment(sketch, "E633", {"start": v(-14.58, -106.44) * mm, "end": v(-11.53, -108.96) * mm});
            skLineSegment(sketch, "E634", {"start": v(-11.53, -108.96) * mm, "end": v(-8.02, -110.87) * mm});
            skLineSegment(sketch, "E635", {"start": v(-8.02, -110.87) * mm, "end": v(-4.15, -112.07) * mm});
            skLineSegment(sketch, "E636", {"start": v(-4.15, -112.07) * mm, "end": v(-1.04, -112.5) * mm});
            skLineSegment(sketch, "E637", {"start": v(-1.04, -112.5) * mm, "end": v(0, -112.5) * mm});
            skLineSegment(sketch, "E638", {"start": v(0, -112.5) * mm, "end": v(1.04, -112.5) * mm});
            skLineSegment(sketch, "E639", {"start": v(1.04, -112.5) * mm, "end": v(4.15, -112.07) * mm});
            skLineSegment(sketch, "E640", {"start": v(4.15, -112.07) * mm, "end": v(8.02, -110.87) * mm});
            skLineSegment(sketch, "E641", {"start": v(8.02, -110.87) * mm, "end": v(11.53, -108.96) * mm});
            skLineSegment(sketch, "E642", {"start": v(11.53, -108.96) * mm, "end": v(14.59, -106.44) * mm});
            skLineSegment(sketch, "E643", {"start": v(14.59, -106.44) * mm, "end": v(17.1, -103.38) * mm});
            skLineSegment(sketch, "E644", {"start": v(17.1, -103.38) * mm, "end": v(19.01, -99.88) * mm});
            skLineSegment(sketch, "E645", {"start": v(19.01, -99.88) * mm, "end": v(20.22, -96) * mm});
            skLineSegment(sketch, "E646", {"start": v(20.22, -96) * mm, "end": v(20.64, -92.9) * mm});
            skLineSegment(sketch, "E647", {"start": v(20.64, -92.9) * mm, "end": v(20.64, -91.85) * mm});
            skLineSegment(sketch, "E648", {"start": v(20.64, -91.85) * mm, "end": v(20.64, -90.81) * mm});
            skLineSegment(sketch, "E649", {"start": v(20.64, -90.81) * mm, "end": v(20.22, -87.7) * mm});
            skLineSegment(sketch, "E650", {"start": v(20.22, -87.7) * mm, "end": v(19.01, -83.83) * mm});
            skLineSegment(sketch, "E651", {"start": v(19.01, -83.83) * mm, "end": v(17.1, -80.33) * mm});
            skLineSegment(sketch, "E652", {"start": v(17.1, -80.33) * mm, "end": v(14.59, -77.27) * mm});
            skLineSegment(sketch, "E653", {"start": v(14.59, -77.27) * mm, "end": v(11.53, -74.75) * mm});
            skLineSegment(sketch, "E654", {"start": v(11.53, -74.75) * mm, "end": v(8.02, -72.84) * mm});
            skLineSegment(sketch, "E655", {"start": v(8.02, -72.84) * mm, "end": v(4.15, -71.64) * mm});
            skLineSegment(sketch, "E656", {"start": v(4.15, -71.64) * mm, "end": v(1.04, -71.22) * mm});
            skLineSegment(sketch, "E657", {"start": v(1.04, -71.22) * mm, "end": v(0, -71.22) * mm});
            skSolve(sketch);
        }
        {
            var Q0;
            Q0=makeQuery(id+"F0.imprint","IMPRINT",FACE,{"disambiguationData":[TD([[makeQuery(id+"F0.imprint","IMPRINT",EDGE,{"derivedFrom":sQuery(id+"F0.wireOp",EDGE,"E0")}),-1.0]])]});
            var Q1;
            Q1=makeQuery(id+"F0.imprint","IMPRINT",FACE,{"disambiguationData":[TD([[makeQuery(id+"F0.imprint","IMPRINT",EDGE,{"derivedFrom":sQuery(id+"F0.wireOp",EDGE,"E360")}),1.0]])]});
            var Q2;
            Q2=makeQuery(id+"F0.imprint","IMPRINT",FACE,{"disambiguationData":[TD([[makeQuery(id+"F0.imprint","IMPRINT",EDGE,{"derivedFrom":sQuery(id+"F0.wireOp",EDGE,"E428")}),1.0]])]});
            var Q3;
            Q3=makeQuery(id+"F0.imprint","IMPRINT",FACE,{"disambiguationData":[TD([[makeQuery(id+"F0.imprint","IMPRINT",EDGE,{"derivedFrom":sQuery(id+"F0.wireOp",EDGE,"E190")}),1.0]])]});
            extrude(context, id + "F1", {"entities" : qUnion([Q0, Q1, Q2, Q3]), "depth" : 3.17 * mm, "offsetDistance" : 25.4 * mm});
        }
        {
            var Q0;
            Q0=makeQuery(id+"F0.imprint","IMPRINT",FACE,{"disambiguationData":[TD([[makeQuery(id+"F0.imprint","IMPRINT",EDGE,{"derivedFrom":sQuery(id+"F0.wireOp",EDGE,"E0")}),-1.0]])]});
            var sketch = newSketch(context, id + "F2", { "sketchPlane" : qUnion([Q0])});
            skCircle(sketch, "E658", {"center": v(215.9, 139.7) * mm, "radius": 3.18 * mm});
            skCircle(sketch, "E659", {"center": v(215.9, -139.7) * mm, "radius": 3.18 * mm});
            skCircle(sketch, "E660", {"center": v(-215.9, -139.7) * mm, "radius": 3.18 * mm});
            skCircle(sketch, "E661", {"center": v(-215.9, 139.7) * mm, "radius": 3.18 * mm});
            skCircle(sketch, "E662", {"center": v(110.1, -1.3) * mm, "radius": 2.38 * mm});
            skCircle(sketch, "E663", {"center": v(70.09, 93.94) * mm, "radius": 2.38 * mm});
            skCircle(sketch, "E664", {"center": v(-9.88, -82.08) * mm, "radius": 2.38 * mm});
            skCircle(sketch, "E665", {"center": v(10.01, -102) * mm, "radius": 2.38 * mm});
            skSolve(sketch);
        }
        {
            var Q0;
            Q0 = qSketchRegion(id + "F2", true);
            extrude(context, id + "F3", {"entities" : qUnion([Q0]), "operationType" : NewBodyOperationType.ADD, "oppositeDirection" : true, "depth" : 25.4 * mm, "offsetDistance" : 25.4 * mm});
        }
        {
            var Q0;
            Q0=makeQuery(id+"F3.opExtrude","CAP_FACE",FACE,{"disambiguationData":[OSD([sQuery(id+"F2.wireOp",EDGE,"E658")])],"isStart":false});
            var sketch = newSketch(context, id + "F4", { "sketchPlane" : qUnion([Q0])});
            skLineSegment(sketch, "E666.bottom", {"start": v(-228.61, 152.4) * mm, "end": v(228.59, 152.4) * mm});
            skLineSegment(sketch, "E666.top", {"start": v(-228.61, -152.4) * mm, "end": v(228.59, -152.4) * mm});
            skLineSegment(sketch, "E666.left", {"start": v(-228.61, 152.4) * mm, "end": v(-228.61, -152.4) * mm});
            skLineSegment(sketch, "E666.right", {"start": v(228.59, 152.4) * mm, "end": v(228.59, -152.4) * mm});
            skSolve(sketch);
        }
        {
            var Q0;
            Q0 = qSketchRegion(id + "F4", true);
            extrude(context, id + "F5", {"entities" : qUnion([Q0]), "depth" : 3.17 * mm, "offsetDistance" : 25.4 * mm});
        }
    });
